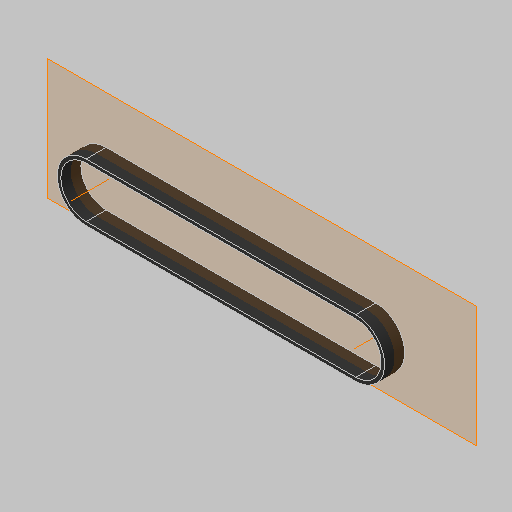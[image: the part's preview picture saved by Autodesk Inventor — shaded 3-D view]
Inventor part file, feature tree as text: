
AUTODESK INVENTOR PART (.ipt)
format: ipt  version: 2023.5 (Build 275446000, 446)  size: 165,376 bytes
history: native  units: in
note: dims shown in document units (in); Inventor stores cm internally (conversion verified against a paired STEP export)
features: sketch x3, extrude x1, other x1, projected_geometry x1
ambient origin geometry x8: Origin, YZ Plane, XZ Plane, XY Plane, X Axis, Y Axis, Z Axis, Center Point
bodies: Body1 (feature_tree)
feature tree (6):
  sketch  "Sketch2"  dims[d0=0.9023in d1=0.9023in]
  extrude  "Extrusion2"  Depth=0.9023in
  sketch  "Sketch5"  dims[d3=1.4174in d5=4.4881in d9=0.0787in d10=0.0598in d11=0.0299in d12=0.0219in d13=0.0219in d14=0.0059in d15=0.0059in d20=0.3346in d21=0.0in d22=0.0787in d23=0.0598in d24=0.0299in d25=0.0219in d26=0.0219in d27=0.0059in d28=0.0059in d29=0.0299in d30=0.0394in d31=0.0787in d32=0.0232in d34=0.0219in d35=0.0in d36=0.0in d37=0.0059in d38=0.0022in d39=0.0022in d40=0.0in d41=0.0in d42=0.0081in d43=0.0081in d44=0.0299in]
  other  "Work Axis1"
  sketch  "Sketch4"  dims[d2=1.4174in]
  projected_geometry  "Projected Loop1"
